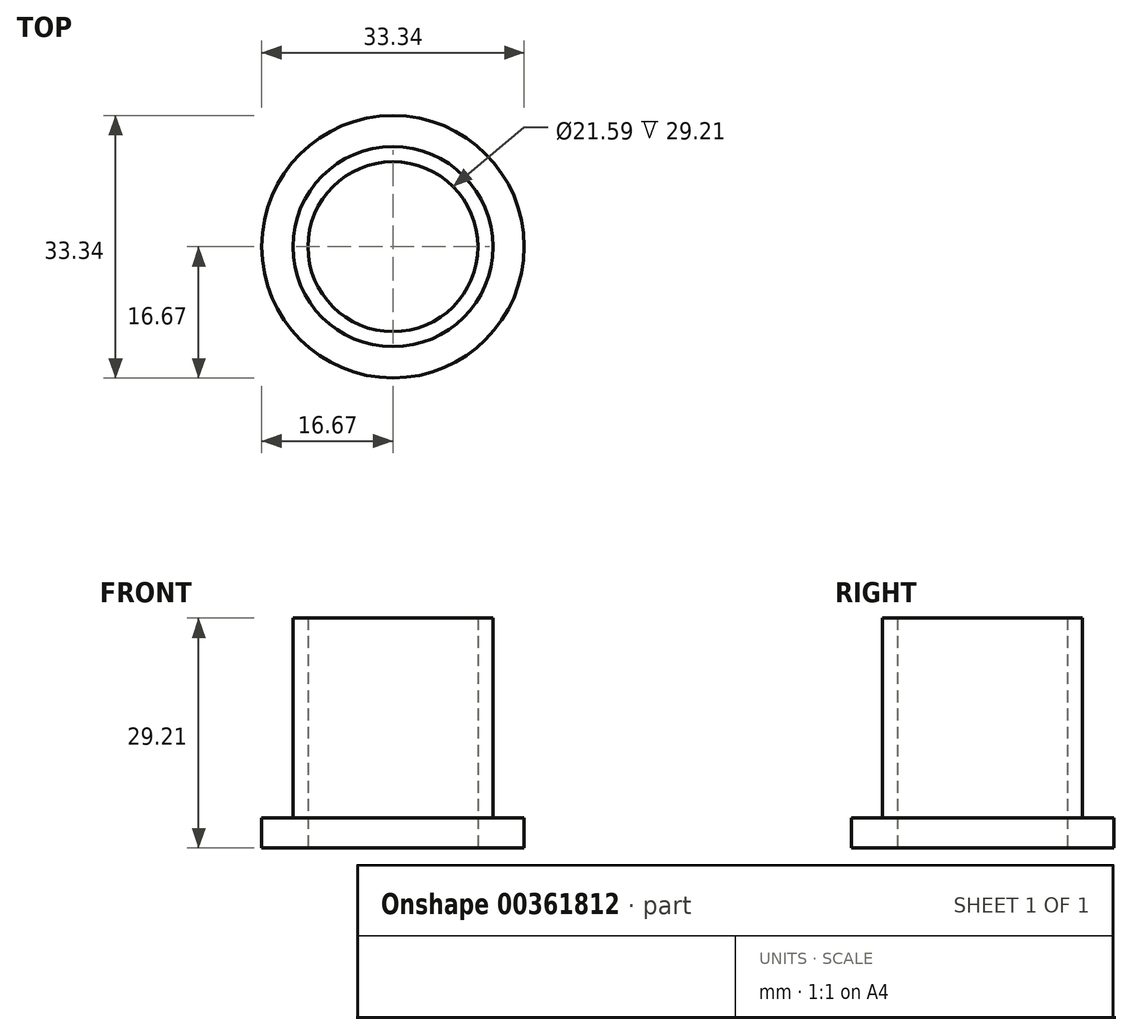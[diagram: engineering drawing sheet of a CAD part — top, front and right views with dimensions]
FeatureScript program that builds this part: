
annotation { "Feature Type Name" : "Feature", "Feature Type Description" : "" }
export const myFeature = defineFeature(function(context is Context, id is Id, definition is map)
    precondition{}
    {
        {
            var Q0;
            Q0=qCreatedBy(makeId("Top.planeOp"),FACE);
            var sketch = newSketch(context, id + "F0", { "sketchPlane" : qUnion([Q0])});
            skCircle(sketch, "E0", {"center": v(0, 0) * mm, "radius": 16.67 * mm});
            skCircle(sketch, "E1", {"center": v(0, 0) * mm, "radius": 12.7 * mm});
            skCircle(sketch, "E2", {"center": v(0, 0) * mm, "radius": 10.8 * mm});
            skSolve(sketch);
        }
        {
            var Q0;
            Q0=makeQuery(id+"F0.imprint","IMPRINT",FACE,{"disambiguationData":[TD([[makeQuery(id+"F0.imprint","IMPRINT",EDGE,{"derivedFrom":sQuery(id+"F0.wireOp",EDGE,"E0")}),1.0]])]});
            extrude(context, id + "F1", {"entities" : qUnion([Q0]), "depth" : 3.8 * mm, "offsetDistance" : 25 * mm});
        }
        {
            var Q0;
            Q0=makeQuery(id+"F0.imprint","IMPRINT",FACE,{"disambiguationData":[TD([[makeQuery(id+"F0.imprint","IMPRINT",EDGE,{"derivedFrom":sQuery(id+"F0.wireOp",EDGE,"E1")}),1.0]])]});
            extrude(context, id + "F2", {"entities" : qUnion([Q0]), "operationType" : NewBodyOperationType.ADD, "depth" : 29.2 * mm});
        }
    });
